# Revit family: SH-7150
name_source: partatom
category: Lighting Fixtures
revit_build: Autodesk Revit 2017 (Build: 20160225_1515(x64)
units: mm (PartAtom-declared; Revit-internal decimal feet)

## family parameters
Cut with Voids When Loaded = No
Host = Face
Light Source = Yes
Part Type = Normal
Room Calculation Point = No
Round Connector Dimension = Use Diameter
Shared = No

## types (2) — shared parameters
Body Material = Aluminum
Color Filter = 16777215
Default Elevation = 122 cm
Diffuser Material = Glass
Dimming Lamp Color Temperature Shift = <None>
IP = IP65
Lamp = LED
Length = 62 cm
Manufacturer = SHOA
Model = SH-7150
Photometric Web File = 50W_IESNA2002(1).IES
Protection Class = Class I
Tilt Angle = 90.00°
Type medule = COB
URL = https://www.shoaco.com
Voltage/Frequency = 230v/50hz
Wattage. = 50 W
Width = 28 cm
color temperature = 3000K-6500K
consumption current = 0 A
website = www.shoaco.com

## type names (no varying parameters)
- SH-7150(Gray color-3000K-LED)
- SH-7150(Gray color-6500K-LED)

## geometry (parser evidence)
native form markers: Sweep x2
no freeform markers — native parametric forms only
